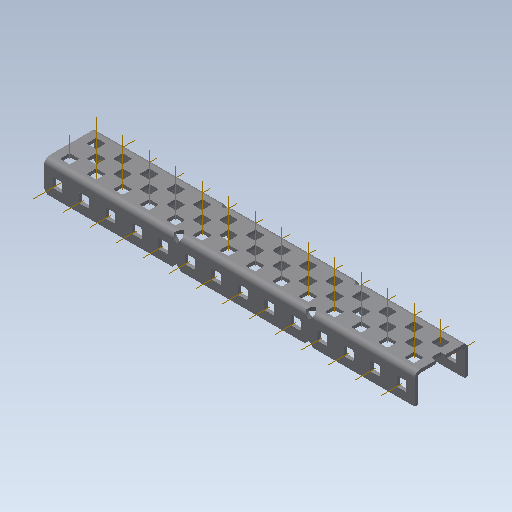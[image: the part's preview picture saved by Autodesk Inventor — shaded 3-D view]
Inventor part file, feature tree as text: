
AUTODESK INVENTOR PART (.ipt)
format: ipt  version: 2020 (Build 240168000, 168)  size: 2,011,136 bytes
history: native  units: in
note: dims shown in document units (in); Inventor stores cm internally (conversion verified against a paired STEP export)
features: other x76, pattern_linear x3, sheet_metal_op x1, extrude x1, imported_body x1, sketch x1
ambient origin geometry x8: Origin, YZ Plane, XZ Plane, XY Plane, X Axis, Y Axis, Z Axis, Center Point
bodies: Body1 (feature_tree)
feature tree (83):
  sheet_metal_op  "Fold1"
  other  "C-Channel"
  extrude  "length cut"  Depth=0.5in
  other  "top axis"
  other  "inner axis"
  other  "front axis"
  other  "back axis"
  pattern_linear  "top axes"  Spacing1=0.5in  [1 undecoded]
  pattern_linear  "inner axes"  Spacing1=0.5in  [1 undecoded]
  pattern_linear  "horiz axes"  Spacing1=-7.0in  [1 undecoded]
  other  "right plane"
  imported_body  "Base1"
  sketch  "Sketch1"  dims[d1=0.0in d4=0.5in d5=0.7874in d7=0.5in d10=0.5in d13=0.5in d14=-7.0in d15=0.0in d16=0.0in d17=0.0in d18=0.0in d19=0.0in]
  other  "Work Point1"
  other  "Work Point2"
  other  "Work Point3"
  other  "Work Point4"
  other  "Work Axis5"
  other  "Work Axis6"
  other  "Work Axis7"
  other  "Work Axis8"
  other  "Work Axis11"
  other  "Work Axis12"
  other  "Work Axis13"
  other  "Work Axis14"
  other  "Work Axis15"
  other  "Work Axis18"
  other  "Work Axis19"
  other  "Work Axis20"
  other  "Work Axis23"
  other  "Work Axis24"
  other  "Work Axis25"
  other  "Work Axis26"
  other  "Work Axis30"
  other  "Work Axis31"
  other  "Work Axis32"
  other  "Work Axis33"
  other  "left plane"
  other  "Work Axis37"
  other  "Work Axis38"
  other  "Work Axis39"
  other  "Work Axis40"
  other  "Work Axis41"
  other  "Work Axis42"
  other  "Work Axis43"
  other  "Work Axis44"
  other  "Work Axis45"
  other  "Work Axis57"
  other  "Work Axis58"
  other  "Work Axis59"
  other  "Work Axis60"
  other  "Work Axis61"
  other  "Work Axis62"
  other  "Work Axis63"
  other  "Work Axis64"
  other  "Work Axis65"
  other  "Work Axis77"
  other  "Work Axis78"
  other  "Work Axis79"
  other  "Work Axis80"
  other  "Work Axis81"
  other  "Work Axis82"
  other  "Work Axis83"
  other  "Work Axis84"
  other  "Work Axis85"
  other  "Work Axis97"
  other  "Work Axis98"
  other  "Work Axis99"
  other  "Work Axis100"
  other  "Work Axis101"
  other  "Work Axis102"
  other  "Work Axis103"
  other  "Work Axis104"
  other  "Work Axis105"
  other  "Work Axis117"
  other  "Work Axis118"
  other  "Work Axis119"
  other  "Work Axis120"
  other  "Work Axis121"
  other  "Work Axis122"
  other  "Work Axis123"
  other  "Work Axis124"
  other  "Work Axis125"
note: 3 required parameter values undecoded (feature->parameter linkage not recoverable at this tier; creation-order binding heuristic only, values carry confidence <= 0.55)
